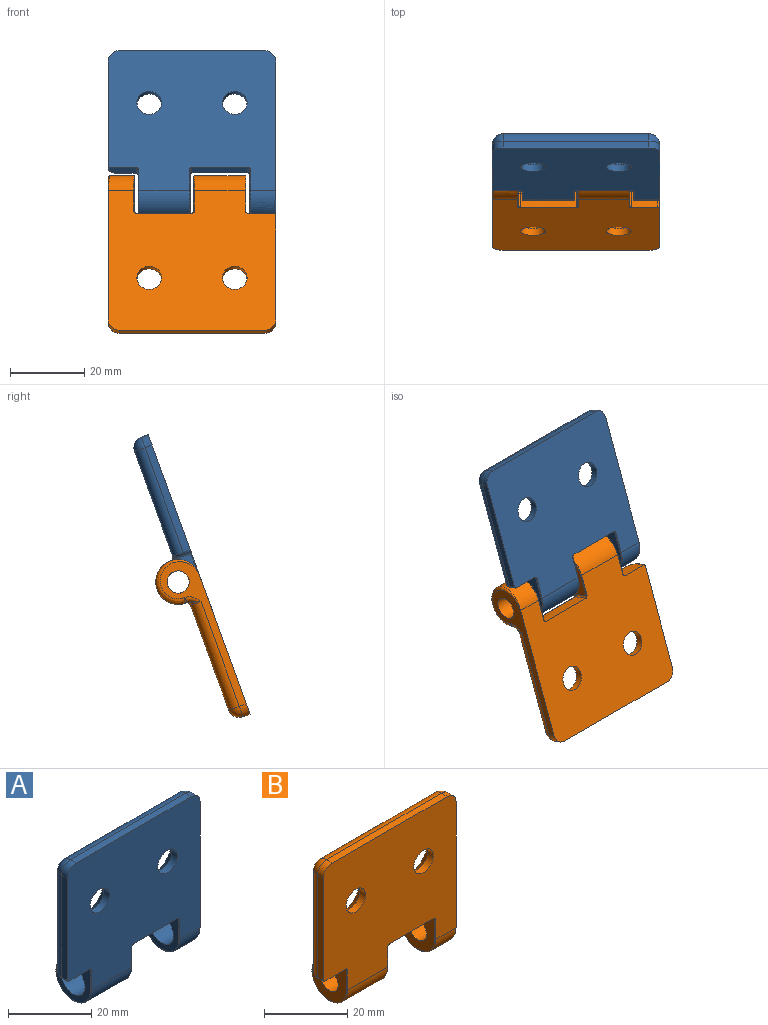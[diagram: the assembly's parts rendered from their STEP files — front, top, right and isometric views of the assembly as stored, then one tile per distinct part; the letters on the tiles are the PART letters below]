
ASSEMBLY  parts=2 mates=1
PART A: 61 faces, bbox 47.8x14.3x47.7 mm
  f0: cylinder r=3.3mm len=6.6mm, axis (0,1,0), area 41.5mm2, adj f1,f14
  f1: cone r=6.94mm half-angle=45deg, axis (0,1,0), area 128mm2, adj f0,f12
  f2: cylinder r=3.3mm len=6.6mm, axis (0,1,0), area 41.5mm2, adj f3,f14
  f3: cone r=6.94mm half-angle=45deg, axis (0,1,0), area 128mm2, adj f2,f12
  f4: torus R=5.8mm, axis (1,0,0), area 8.8mm2, adj f15,f17,f41,f42
  f5: torus R=5.8mm, axis (1,0,0), area 8.8mm2, adj f9,f20,f38,f39
  f6: cylinder r=4mm len=14mm, axis (-1,0,0), area 351.9mm2, adj f18,f20
  f7: cylinder r=4mm len=8mm, axis (-1,0,0), area 175.9mm2, adj f10,f17
  f8: plane 1.5x0.29mm, normal (0,0,1), area 0.1mm2, adj f15,f30,f36
  f9: cylinder r=6mm len=13.6mm, axis (-1,0,0), area 384.5mm2, adj f5,f14,f31,f44
  f10: plane 43.52x11.95mm, normal (1,0,0), area 105.7mm2, adj f7,f14,f21,f27,f35,f36,f37
  f11: plane 30x2mm, normal (-1,0,0), area 60mm2, adj f14,f22,f23,f34
  f12: plane 39x30mm, normal (0,1,0), area 912.4mm2, adj f1,f3,f23,f25,f27,f28,f29,f31
  f13: plane 39x2mm, normal (0,0,1), area 78mm2, adj f14,f21,f22,f25
  f14: plane 45x40mm, normal (0,-1,0), area 1568.1mm2, adj f0,f2,f9,f10,f11,f13,f15,f16
  f15: cylinder r=6mm len=12mm, axis (-1,0,0), area 171.1mm2, adj f4,f8,f14,f29,f35
  f16: plane 15.06x4mm, normal (0,0,-1), area 60mm2, adj f14,f28,f54,f55,f59,f60
  f17: plane 12.17x11.6mm, normal (-1,0,0), area 63.9mm2, adj f4,f7,f41,f42,f53,f54
  f18: plane 12.17x11.6mm, normal (1,0,0), area 63.9mm2, adj f6,f43,f44,f45,f58,f59
  f19: plane 7.03x4.5mm, normal (0,0,-1), area 30.2mm2, adj f14,f32,f33,f34,f49,f50
  f20: plane 12x11.6mm, normal (-1,0,0), area 63.8mm2, adj f5,f6,f38,f39,f48,f49
  f21: cylinder r=3mm len=3mm, axis (0,1,0), area 9.4mm2, adj f10,f13,f14,f26
  f22: cylinder r=3mm len=3mm, axis (0,-1,0), area 9.4mm2, adj f11,f13,f14,f24
  f23: cylinder r=3mm len=30mm, axis (0,0,1), area 141.4mm2, adj f11,f12,f24,f33
  f24: sphere r=3mm, area 14.1mm2, adj f22,f23,f25
  f25: cylinder r=3mm len=39mm, axis (-1,0,0), area 183.8mm2, adj f12,f13,f24,f26
  f26: sphere r=3mm, area 14.1mm2, adj f21,f25,f27
  f27: cylinder r=3mm len=30mm, axis (0,0,-1), area 141.4mm2, adj f10,f12,f26,f30
  f28: cylinder r=1mm len=16.4mm, axis (-1,0,0), area 24.1mm2, adj f12,f16,f51,f52,f53,f56,f57,f58
  f29: cylinder r=1mm len=3.8mm, axis (1,0,0), area 6mm2, adj f12,f15,f30,f41
  f30: torus R=4mm, axis (0,0,-1), area 5mm2, adj f8,f27,f29,f37
  f31: cylinder r=1mm len=13.6mm, axis (1,0,0), area 21.4mm2, adj f9,f12,f38,f45
  f32: cylinder r=0.5mm len=5.2mm, axis (-1,0,0), area 3.7mm2, adj f12,f19,f33,f47,f48
  f33: torus R=2.5mm, axis (0,0,1), area 3.5mm2, adj f19,f23,f32,f34
  f34: cylinder r=0.5mm len=2mm, axis (0,-1,0), area 1.6mm2, adj f11,f14,f19,f33
  f35: bspline ~12.03x12.03mm, area 25.5mm2, adj f10,f15,f36
  f36: cylinder r=1.5mm len=1.5mm, axis (0,1,0), area 0.7mm2, adj f8,f10,f35,f37
  f37: bspline ~3.71x2.5mm, area 3.4mm2, adj f10,f30,f36
  f38: torus R=1.2mm, axis (1,0,0), area 0.4mm2, adj f5,f20,f31,f47
  f39: cylinder r=0.2mm len=6mm, axis (0,0,-1), area 1.9mm2, adj f5,f14,f20,f50
  f40: cylinder r=0.2mm len=0.5mm, axis (0,0,1), area 0mm2, adj f12,f41,f51
  f41: torus R=1.2mm, axis (1,0,0), area 0.4mm2, adj f4,f17,f29,f40,f52
  f42: cylinder r=0.2mm len=6mm, axis (0,0,-1), area 1.9mm2, adj f4,f14,f17,f55
  f43: cylinder r=0.2mm len=6mm, axis (0,0,1), area 1.9mm2, adj f14,f18,f44,f60
  f44: torus R=5.8mm, axis (-1,0,0), area 8.8mm2, adj f9,f18,f43,f45
  f45: torus R=1.2mm, axis (-1,0,0), area 0.4mm2, adj f18,f31,f44,f46,f57
  f46: cylinder r=0.2mm len=0.5mm, axis (0,0,-1), area 0mm2, adj f12,f45,f56
  f47: bspline ~0.8x0.7mm, area 0.1mm2, adj f32,f38,f48
  f48: torus R=1mm, axis (1,0,0), area 0.3mm2, adj f20,f32,f47,f49
  f49: cylinder r=0.5mm len=4.3mm, axis (0,-1,0), area 3.4mm2, adj f19,f20,f48,f50
  f50: torus R=0.7mm, axis (0,0,1), area 0.2mm2, adj f14,f19,f39,f49
  f51: bspline ~0.5x0.34mm, area 0mm2, adj f28,f40,f52
  f52: bspline ~0.8x0.6mm, area 0.3mm2, adj f28,f41,f51,f53
  f53: torus R=1.5mm, axis (1,0,0), area 0.7mm2, adj f17,f28,f52,f54
  f54: cylinder r=0.5mm len=3.8mm, axis (0,-1,0), area 3mm2, adj f16,f17,f53,f55
  f55: torus R=0.7mm, axis (0,0,1), area 0.2mm2, adj f14,f16,f42,f54
  f56: bspline ~0.5x0.34mm, area 0mm2, adj f28,f46,f57
  f57: bspline ~0.8x0.6mm, area 0.3mm2, adj f28,f45,f56,f58
  f58: torus R=1.5mm, axis (-1,0,0), area 0.7mm2, adj f18,f28,f57,f59
  f59: cylinder r=0.5mm len=3.8mm, axis (0,-1,0), area 3mm2, adj f16,f18,f58,f60
  f60: torus R=0.7mm, axis (0,0,1), area 0.2mm2, adj f14,f16,f43,f59
PART B: 61 faces, bbox 47.8x14.3x47.7 mm
  f0: cylinder r=3.3mm len=6.6mm, axis (0,1,0), area 41.5mm2, adj f1,f14
  f1: cone r=6.94mm half-angle=45deg, axis (0,1,0), area 128mm2, adj f0,f12
  f2: cylinder r=3.3mm len=6.6mm, axis (0,1,0), area 41.5mm2, adj f3,f14
  f3: cone r=6.94mm half-angle=45deg, axis (0,1,0), area 128mm2, adj f2,f12
  f4: torus R=5.8mm, axis (1,0,0), area 8.8mm2, adj f15,f17,f41,f42
  f5: torus R=5.8mm, axis (1,0,0), area 8.8mm2, adj f9,f20,f38,f39
  f6: cylinder r=3mm len=14mm, axis (-1,0,0), area 263.9mm2, adj f18,f20
  f7: cylinder r=3mm len=7mm, axis (-1,0,0), area 131.9mm2, adj f10,f17
  f8: plane 1.5x0.29mm, normal (0,0,1), area 0.1mm2, adj f15,f30,f36
  f9: cylinder r=6mm len=13.6mm, axis (-1,0,0), area 384.5mm2, adj f5,f14,f31,f44
  f10: plane 43.52x11.95mm, normal (1,0,0), area 127.7mm2, adj f7,f14,f21,f27,f35,f36,f37
  f11: plane 30x2mm, normal (-1,0,0), area 60mm2, adj f14,f22,f23,f34
  f12: plane 39x30mm, normal (0,1,0), area 912.4mm2, adj f1,f3,f23,f25,f27,f28,f29,f31
  f13: plane 39x2mm, normal (0,0,1), area 78mm2, adj f14,f21,f22,f25
  f14: plane 45x40mm, normal (0,-1,0), area 1568.1mm2, adj f0,f2,f9,f10,f11,f13,f15,f16
  f15: cylinder r=6mm len=12mm, axis (-1,0,0), area 171.1mm2, adj f4,f8,f14,f29,f35
  f16: plane 15.06x4mm, normal (0,0,-1), area 60mm2, adj f14,f28,f54,f55,f59,f60
  f17: plane 12.17x11.6mm, normal (-1,0,0), area 85.9mm2, adj f4,f7,f41,f42,f53,f54
  f18: plane 12.17x11.6mm, normal (1,0,0), area 85.9mm2, adj f6,f43,f44,f45,f58,f59
  f19: plane 7.03x4.5mm, normal (0,0,-1), area 30.2mm2, adj f14,f32,f33,f34,f49,f50
  f20: plane 12x11.6mm, normal (-1,0,0), area 85.8mm2, adj f5,f6,f38,f39,f48,f49
  f21: cylinder r=3mm len=3mm, axis (0,1,0), area 9.4mm2, adj f10,f13,f14,f26
  f22: cylinder r=3mm len=3mm, axis (0,-1,0), area 9.4mm2, adj f11,f13,f14,f24
  f23: cylinder r=3mm len=30mm, axis (0,0,1), area 141.4mm2, adj f11,f12,f24,f33
  f24: sphere r=3mm, area 14.1mm2, adj f22,f23,f25
  f25: cylinder r=3mm len=39mm, axis (-1,0,0), area 183.8mm2, adj f12,f13,f24,f26
  f26: sphere r=3mm, area 14.1mm2, adj f21,f25,f27
  f27: cylinder r=3mm len=30mm, axis (0,0,-1), area 141.4mm2, adj f10,f12,f26,f30
  f28: cylinder r=1mm len=16.4mm, axis (-1,0,0), area 24.1mm2, adj f12,f16,f51,f52,f53,f56,f57,f58
  f29: cylinder r=1mm len=3.8mm, axis (1,0,0), area 6mm2, adj f12,f15,f30,f41
  f30: torus R=4mm, axis (0,0,-1), area 5mm2, adj f8,f27,f29,f37
  f31: cylinder r=1mm len=13.6mm, axis (1,0,0), area 21.4mm2, adj f9,f12,f38,f45
  f32: cylinder r=0.5mm len=5.2mm, axis (-1,0,0), area 3.7mm2, adj f12,f19,f33,f47,f48
  f33: torus R=2.5mm, axis (0,0,1), area 3.5mm2, adj f19,f23,f32,f34
  f34: cylinder r=0.5mm len=2mm, axis (0,-1,0), area 1.6mm2, adj f11,f14,f19,f33
  f35: bspline ~12.03x12.03mm, area 25.5mm2, adj f10,f15,f36
  f36: cylinder r=1.5mm len=1.5mm, axis (0,1,0), area 0.7mm2, adj f8,f10,f35,f37
  f37: bspline ~3.71x2.5mm, area 3.4mm2, adj f10,f30,f36
  f38: torus R=1.2mm, axis (1,0,0), area 0.4mm2, adj f5,f20,f31,f47
  f39: cylinder r=0.2mm len=6mm, axis (0,0,-1), area 1.9mm2, adj f5,f14,f20,f50
  f40: cylinder r=0.2mm len=0.5mm, axis (0,0,1), area 0mm2, adj f12,f41,f51
  f41: torus R=1.2mm, axis (1,0,0), area 0.4mm2, adj f4,f17,f29,f40,f52
  f42: cylinder r=0.2mm len=6mm, axis (0,0,-1), area 1.9mm2, adj f4,f14,f17,f55
  f43: cylinder r=0.2mm len=6mm, axis (0,0,1), area 1.9mm2, adj f14,f18,f44,f60
  f44: torus R=5.8mm, axis (-1,0,0), area 8.8mm2, adj f9,f18,f43,f45
  f45: torus R=1.2mm, axis (-1,0,0), area 0.4mm2, adj f18,f31,f44,f46,f57
  f46: cylinder r=0.2mm len=0.5mm, axis (0,0,-1), area 0mm2, adj f12,f45,f56
  f47: bspline ~0.8x0.7mm, area 0.1mm2, adj f32,f38,f48
  f48: torus R=1mm, axis (1,0,0), area 0.3mm2, adj f20,f32,f47,f49
  f49: cylinder r=0.5mm len=4.3mm, axis (0,-1,0), area 3.4mm2, adj f19,f20,f48,f50
  f50: torus R=0.7mm, axis (0,0,1), area 0.2mm2, adj f14,f19,f39,f49
  f51: bspline ~0.5x0.34mm, area 0mm2, adj f28,f40,f52
  f52: bspline ~0.8x0.6mm, area 0.3mm2, adj f28,f41,f51,f53
  f53: torus R=1.5mm, axis (1,0,0), area 0.7mm2, adj f17,f28,f52,f54
  f54: cylinder r=0.5mm len=3.8mm, axis (0,-1,0), area 3mm2, adj f16,f17,f53,f55
  f55: torus R=0.7mm, axis (0,0,1), area 0.2mm2, adj f14,f16,f42,f54
  f56: bspline ~0.5x0.34mm, area 0mm2, adj f28,f46,f57
  f57: bspline ~0.8x0.6mm, area 0.3mm2, adj f28,f45,f56,f58
  f58: torus R=1.5mm, axis (-1,0,0), area 0.7mm2, adj f18,f28,f57,f59
  f59: cylinder r=0.5mm len=3.8mm, axis (0,-1,0), area 3mm2, adj f16,f18,f58,f60
  f60: torus R=0.7mm, axis (0,0,1), area 0.2mm2, adj f14,f16,f43,f59
PLACE A rot(axis=(-1,0,0),20deg) t=(-28.15,11.9,-3.41)mm
PLACE B rot(axis=(0,-0.98,0.17),180deg) t=(-28.15,11.9,-3.41)mm
MATE revolute A.f4 <-> B.f4  axis (-1,0,0) through (-28.65,11.9,-3.41)mm
